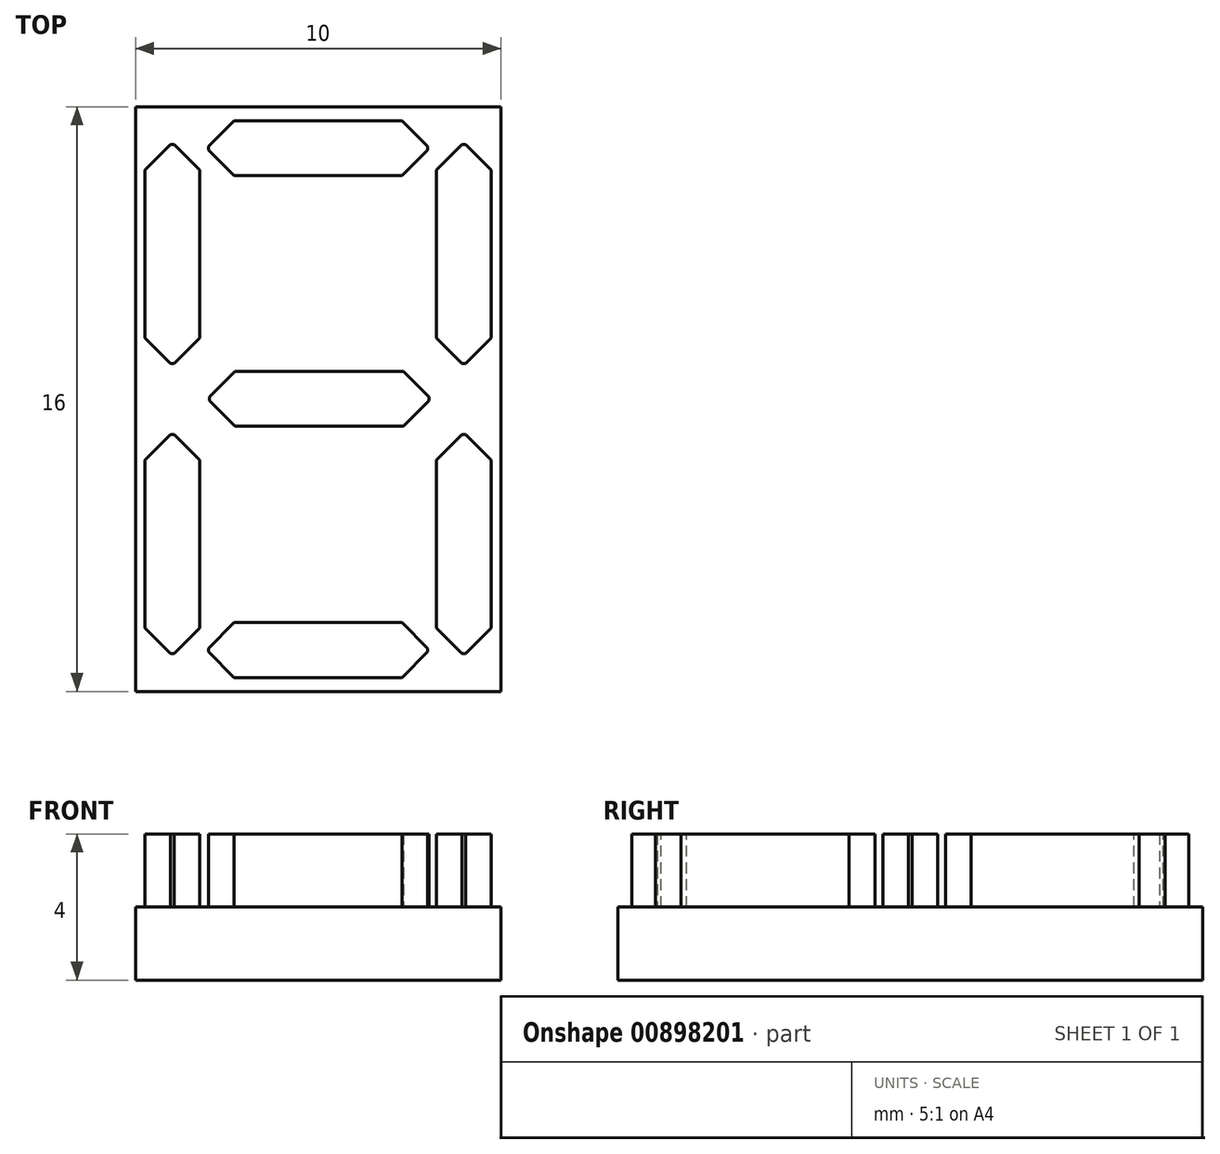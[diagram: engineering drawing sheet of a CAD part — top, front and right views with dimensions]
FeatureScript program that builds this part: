
annotation { "Feature Type Name" : "Feature", "Feature Type Description" : "" }
export const myFeature = defineFeature(function(context is Context, id is Id, definition is map)
    precondition{}
    {
        {
            var Q0;
            Q0=qCreatedBy(makeId("Top.planeOp"),FACE);
            var sketch = newSketch(context, id + "F0", { "sketchPlane" : qUnion([Q0])});
            skLineSegment(sketch, "E0.bottom", {"start": v(5, -8) * mm, "end": v(-5, -8) * mm});
            skLineSegment(sketch, "E0.top", {"start": v(5, 8) * mm, "end": v(-5, 8) * mm});
            skLineSegment(sketch, "E0.left", {"start": v(5, -8) * mm, "end": v(5, 8) * mm});
            skLineSegment(sketch, "E0.right", {"start": v(-5, -8) * mm, "end": v(-5, 8) * mm});
            skPoint(sketch, "E0.middle", {"position": v(0, 0) * mm});
            skSolve(sketch);
        }
        {
            var Q0;
            Q0 = qSketchRegion(id + "F0", true);
            extrude(context, id + "F1", {"entities" : qUnion([Q0]), "oppositeDirection" : true, "depth" : 2 * mm, "offsetDistance" : 25 * mm});
        }
        {
            var Q0;
            Q0=makeQuery(id+"F1.opExtrude","CAP_FACE",FACE,{"disambiguationData":[OSD([sQuery(id+"F0.wireOp",EDGE,"E0.bottom"),sQuery(id+"F0.wireOp",EDGE,"E0.top"),sQuery(id+"F0.wireOp",EDGE,"E0.left"),sQuery(id+"F0.wireOp",EDGE,"E0.right")])],"isStart":true});
            var sketch = newSketch(context, id + "F2", { "sketchPlane" : qUnion([Q0])});
            skLineSegment(sketch, "E1", {"start": v(0, 8) * mm, "end": v(0, -8) * mm, "construction": true});
            skLineSegment(sketch, "E2", {"start": v(-5, 0) * mm, "end": v(5, 0) * mm, "construction": true});
            skLineSegment(sketch, "E3.bottom", {"start": v(3, 6.12) * mm, "end": v(-3, 6.12) * mm});
            skLineSegment(sketch, "E3.top", {"start": v(3, 7.62) * mm, "end": v(-3, 7.62) * mm});
            skLineSegment(sketch, "E3.left", {"start": v(3, 6.12) * mm, "end": v(3, 7.62) * mm});
            skLineSegment(sketch, "E3.right", {"start": v(-3, 6.12) * mm, "end": v(-3, 7.62) * mm});
            skPoint(sketch, "E3.middle", {"position": v(0, 6.87) * mm});
            skLineSegment(sketch, "E4.MirrorCS", {"start": v(-3, -6.12) * mm, "end": v(-3, -7.62) * mm});
            skLineSegment(sketch, "E5.MirrorCS", {"start": v(3, -6.12) * mm, "end": v(3, -7.62) * mm});
            skPoint(sketch, "E6.MirrorP", {"position": v(0, -6.87) * mm});
            skLineSegment(sketch, "E7.MirrorCS", {"start": v(3, -6.12) * mm, "end": v(-3, -6.12) * mm});
            skLineSegment(sketch, "E8.MirrorCS", {"start": v(4.74, -6.97) * mm, "end": v(4.74, -0.97) * mm});
            skLineSegment(sketch, "E9.MirrorCS", {"start": v(3, -7.62) * mm, "end": v(-3, -7.62) * mm});
            skLineSegment(sketch, "E10.MirrorCS", {"start": v(3.24, -6.97) * mm, "end": v(3.24, -0.47) * mm});
            skLineSegment(sketch, "E11.MirrorCS", {"start": v(3.24, -0.97) * mm, "end": v(4.74, -0.97) * mm});
            skLineSegment(sketch, "E12.MirrorCS", {"start": v(3.24, -6.97) * mm, "end": v(4.74, -6.97) * mm});
            skPoint(sketch, "E13.middle", {"position": v(0, 0) * mm});
            skLineSegment(sketch, "E14.MirrorCS", {"start": v(-4.74, -6.97) * mm, "end": v(-4.74, -0.97) * mm});
            skLineSegment(sketch, "E15.MirrorCS", {"start": v(-3.24, -0.97) * mm, "end": v(-4.74, -0.97) * mm});
            skLineSegment(sketch, "E16.MirrorCS", {"start": v(-3.24, -6.97) * mm, "end": v(-3.24, -0.47) * mm});
            skLineSegment(sketch, "E17.MirrorCS", {"start": v(-3.24, -6.97) * mm, "end": v(-4.74, -6.97) * mm});
            skLineSegment(sketch, "E18.MirrorCS", {"start": v(-3.24, 0.97) * mm, "end": v(-4.74, 0.97) * mm});
            skLineSegment(sketch, "E19.MirrorCS", {"start": v(4.74, 6.97) * mm, "end": v(4.74, 0.97) * mm});
            skLineSegment(sketch, "E20.MirrorCS", {"start": v(3.24, 0.97) * mm, "end": v(4.74, 0.97) * mm});
            skLineSegment(sketch, "E21.MirrorCS", {"start": v(3.24, 6.97) * mm, "end": v(4.74, 6.97) * mm});
            skLineSegment(sketch, "E22.MirrorCS", {"start": v(-4.74, 6.97) * mm, "end": v(-4.74, 0.97) * mm});
            skLineSegment(sketch, "E23.MirrorCS", {"start": v(3.24, 6.97) * mm, "end": v(3.24, 0.47) * mm});
            skLineSegment(sketch, "E24.MirrorCS", {"start": v(-3.24, 6.97) * mm, "end": v(-3.24, 0.47) * mm});
            skLineSegment(sketch, "E25.MirrorCS", {"start": v(-3.24, 6.97) * mm, "end": v(-4.74, 6.97) * mm});
            skLineSegment(sketch, "E26.MirrorCS", {"start": v(-2.97, 0.76) * mm, "end": v(-2.97, -0.74) * mm});
            skLineSegment(sketch, "E27.MirrorCS", {"start": v(3.03, 0.76) * mm, "end": v(3.03, -0.74) * mm});
            skLineSegment(sketch, "E28.MirrorCS", {"start": v(3.03, 0.76) * mm, "end": v(-2.97, 0.76) * mm});
            skLineSegment(sketch, "E29.MirrorCS", {"start": v(3.03, -0.74) * mm, "end": v(-2.97, -0.74) * mm});
            skSolve(sketch);
        }
        {
            var Q0;
            Q0=makeQuery(id+"F2.imprint","IMPRINT",FACE,{"disambiguationData":[TD([[makeQuery(id+"F2.imprint","IMPRINT",EDGE,{"derivedFrom":sQuery(id+"F2.wireOp",EDGE,"E18.MirrorCS")}),-1.0]])]});
            var Q1;
            Q1=makeQuery(id+"F2.imprint","IMPRINT",FACE,{"disambiguationData":[TD([[makeQuery(id+"F2.imprint","IMPRINT",EDGE,{"derivedFrom":sQuery(id+"F2.wireOp",EDGE,"E3.top")}),1.0]])]});
            var Q2;
            Q2=makeQuery(id+"F2.imprint","IMPRINT",FACE,{"disambiguationData":[TD([[makeQuery(id+"F2.imprint","IMPRINT",EDGE,{"derivedFrom":sQuery(id+"F2.wireOp",EDGE,"E19.MirrorCS")}),-1.0]])]});
            var Q3;
            Q3=makeQuery(id+"F2.imprint","IMPRINT",FACE,{"disambiguationData":[TD([[makeQuery(id+"F2.imprint","IMPRINT",EDGE,{"derivedFrom":sQuery(id+"F2.wireOp",EDGE,"E26.MirrorCS")}),1.0]])]});
            var Q4;
            Q4=makeQuery(id+"F2.imprint","IMPRINT",FACE,{"disambiguationData":[TD([[makeQuery(id+"F2.imprint","IMPRINT",EDGE,{"derivedFrom":sQuery(id+"F2.wireOp",EDGE,"E14.MirrorCS")}),-1.0]])]});
            var Q5;
            Q5=makeQuery(id+"F2.imprint","IMPRINT",FACE,{"disambiguationData":[TD([[makeQuery(id+"F2.imprint","IMPRINT",EDGE,{"derivedFrom":sQuery(id+"F2.wireOp",EDGE,"E4.MirrorCS")}),1.0]])]});
            var Q6;
            Q6=makeQuery(id+"F2.imprint","IMPRINT",FACE,{"disambiguationData":[TD([[makeQuery(id+"F2.imprint","IMPRINT",EDGE,{"derivedFrom":sQuery(id+"F2.wireOp",EDGE,"E8.MirrorCS")}),1.0]])]});
            extrude(context, id + "F3", {"entities" : qUnion([Q0, Q1, Q2, Q3, Q4, Q5, Q6]), "operationType" : NewBodyOperationType.ADD, "depth" : 2 * mm, "offsetDistance" : 25 * mm});
        }
        {
            var Q0;
            Q0=makeQuery(id+"F3.opExtrude","SWEPT_EDGE",EDGE,{"disambiguationData":[OSD([sQuery(id+"F2.wireOp",EDGE,"E3.left"),sQuery(id+"F2.wireOp",EDGE,"E3.bottom")])]});
            var Q1;
            Q1=makeQuery(id+"F3.opExtrude","SWEPT_EDGE",EDGE,{"disambiguationData":[OSD([sQuery(id+"F2.wireOp",EDGE,"E21.MirrorCS"),sQuery(id+"F2.wireOp",EDGE,"E23.MirrorCS")])]});
            var Q2;
            Q2=makeQuery(id+"F3.opExtrude","SWEPT_EDGE",EDGE,{"disambiguationData":[OSD([sQuery(id+"F2.wireOp",EDGE,"E20.MirrorCS"),sQuery(id+"F2.wireOp",EDGE,"E23.MirrorCS")])]});
            var Q3;
            Q3=makeQuery(id+"F3.opExtrude","SWEPT_EDGE",EDGE,{"disambiguationData":[OSD([sQuery(id+"F2.wireOp",EDGE,"E19.MirrorCS"),sQuery(id+"F2.wireOp",EDGE,"E20.MirrorCS")])]});
            var Q4;
            Q4=makeQuery(id+"F3.opExtrude","SWEPT_EDGE",EDGE,{"disambiguationData":[OSD([sQuery(id+"F2.wireOp",EDGE,"E10.MirrorCS"),sQuery(id+"F2.wireOp",EDGE,"E11.MirrorCS")])]});
            var Q5;
            Q5=makeQuery(id+"F3.opExtrude","SWEPT_EDGE",EDGE,{"disambiguationData":[OSD([sQuery(id+"F2.wireOp",EDGE,"E27.MirrorCS"),sQuery(id+"F2.wireOp",EDGE,"E29.MirrorCS")])]});
            var Q6;
            Q6=makeQuery(id+"F3.opExtrude","SWEPT_EDGE",EDGE,{"disambiguationData":[OSD([sQuery(id+"F2.wireOp",EDGE,"E26.MirrorCS"),sQuery(id+"F2.wireOp",EDGE,"E29.MirrorCS")])]});
            var Q7;
            Q7=makeQuery(id+"F3.opExtrude","SWEPT_EDGE",EDGE,{"disambiguationData":[OSD([sQuery(id+"F2.wireOp",EDGE,"E26.MirrorCS"),sQuery(id+"F2.wireOp",EDGE,"E28.MirrorCS")])]});
            var Q8;
            Q8=makeQuery(id+"F3.opExtrude","SWEPT_EDGE",EDGE,{"disambiguationData":[OSD([sQuery(id+"F2.wireOp",EDGE,"E18.MirrorCS"),sQuery(id+"F2.wireOp",EDGE,"E24.MirrorCS")])]});
            var Q9;
            Q9=makeQuery(id+"F3.opExtrude","SWEPT_EDGE",EDGE,{"disambiguationData":[OSD([sQuery(id+"F2.wireOp",EDGE,"E18.MirrorCS"),sQuery(id+"F2.wireOp",EDGE,"E22.MirrorCS")])]});
            var Q10;
            Q10=makeQuery(id+"F3.opExtrude","SWEPT_EDGE",EDGE,{"disambiguationData":[OSD([sQuery(id+"F2.wireOp",EDGE,"E22.MirrorCS"),sQuery(id+"F2.wireOp",EDGE,"E25.MirrorCS")])]});
            var Q11;
            Q11=makeQuery(id+"F3.opExtrude","SWEPT_EDGE",EDGE,{"disambiguationData":[OSD([sQuery(id+"F2.wireOp",EDGE,"E3.right"),sQuery(id+"F2.wireOp",EDGE,"E3.bottom")])]});
            var Q12;
            Q12=makeQuery(id+"F3.opExtrude","SWEPT_EDGE",EDGE,{"disambiguationData":[OSD([sQuery(id+"F2.wireOp",EDGE,"E3.top"),sQuery(id+"F2.wireOp",EDGE,"E3.right")])]});
            var Q13;
            Q13=makeQuery(id+"F3.opExtrude","SWEPT_EDGE",EDGE,{"disambiguationData":[OSD([sQuery(id+"F2.wireOp",EDGE,"E10.MirrorCS"),sQuery(id+"F2.wireOp",EDGE,"E12.MirrorCS")])]});
            var Q14;
            Q14=makeQuery(id+"F3.opExtrude","SWEPT_EDGE",EDGE,{"disambiguationData":[OSD([sQuery(id+"F2.wireOp",EDGE,"E8.MirrorCS"),sQuery(id+"F2.wireOp",EDGE,"E12.MirrorCS")])]});
            var Q15;
            Q15=makeQuery(id+"F3.opExtrude","SWEPT_EDGE",EDGE,{"disambiguationData":[OSD([sQuery(id+"F2.wireOp",EDGE,"E5.MirrorCS"),sQuery(id+"F2.wireOp",EDGE,"E9.MirrorCS")])]});
            var Q16;
            Q16=makeQuery(id+"F3.opExtrude","SWEPT_EDGE",EDGE,{"disambiguationData":[OSD([sQuery(id+"F2.wireOp",EDGE,"E4.MirrorCS"),sQuery(id+"F2.wireOp",EDGE,"E9.MirrorCS")])]});
            var Q17;
            Q17=makeQuery(id+"F3.opExtrude","SWEPT_EDGE",EDGE,{"disambiguationData":[OSD([sQuery(id+"F2.wireOp",EDGE,"E16.MirrorCS"),sQuery(id+"F2.wireOp",EDGE,"E17.MirrorCS")])]});
            var Q18;
            Q18=makeQuery(id+"F3.opExtrude","SWEPT_EDGE",EDGE,{"disambiguationData":[OSD([sQuery(id+"F2.wireOp",EDGE,"E14.MirrorCS"),sQuery(id+"F2.wireOp",EDGE,"E17.MirrorCS")])]});
            var Q19;
            Q19=makeQuery(id+"F3.opExtrude","SWEPT_EDGE",EDGE,{"disambiguationData":[OSD([sQuery(id+"F2.wireOp",EDGE,"E4.MirrorCS"),sQuery(id+"F2.wireOp",EDGE,"E7.MirrorCS")])]});
            var Q20;
            Q20=makeQuery(id+"F3.opExtrude","SWEPT_EDGE",EDGE,{"disambiguationData":[OSD([sQuery(id+"F2.wireOp",EDGE,"E14.MirrorCS"),sQuery(id+"F2.wireOp",EDGE,"E15.MirrorCS")])]});
            var Q21;
            Q21=makeQuery(id+"F3.opExtrude","SWEPT_EDGE",EDGE,{"disambiguationData":[OSD([sQuery(id+"F2.wireOp",EDGE,"E15.MirrorCS"),sQuery(id+"F2.wireOp",EDGE,"E16.MirrorCS")])]});
            var Q22;
            Q22=makeQuery(id+"F3.opExtrude","SWEPT_EDGE",EDGE,{"disambiguationData":[OSD([sQuery(id+"F2.wireOp",EDGE,"E27.MirrorCS"),sQuery(id+"F2.wireOp",EDGE,"E28.MirrorCS")])]});
            var Q23;
            Q23=makeQuery(id+"F3.opExtrude","SWEPT_EDGE",EDGE,{"disambiguationData":[OSD([sQuery(id+"F2.wireOp",EDGE,"E8.MirrorCS"),sQuery(id+"F2.wireOp",EDGE,"E11.MirrorCS")])]});
            var Q24;
            Q24=makeQuery(id+"F3.opExtrude","SWEPT_EDGE",EDGE,{"disambiguationData":[OSD([sQuery(id+"F2.wireOp",EDGE,"E5.MirrorCS"),sQuery(id+"F2.wireOp",EDGE,"E7.MirrorCS")])]});
            var Q25;
            Q25=makeQuery(id+"F3.opExtrude","SWEPT_EDGE",EDGE,{"disambiguationData":[OSD([sQuery(id+"F2.wireOp",EDGE,"E19.MirrorCS"),sQuery(id+"F2.wireOp",EDGE,"E21.MirrorCS")])]});
            var Q26;
            Q26=makeQuery(id+"F3.opExtrude","SWEPT_EDGE",EDGE,{"disambiguationData":[OSD([sQuery(id+"F2.wireOp",EDGE,"E3.top"),sQuery(id+"F2.wireOp",EDGE,"E3.left")])]});
            var Q27;
            Q27=makeQuery(id+"F3.opExtrude","SWEPT_EDGE",EDGE,{"disambiguationData":[OSD([sQuery(id+"F2.wireOp",EDGE,"E24.MirrorCS"),sQuery(id+"F2.wireOp",EDGE,"E25.MirrorCS")])]});
            chamfer(context, id + "F4", {"entities" : qUnion([Q0, Q1, Q2, Q3, Q4, Q5, Q6, Q7, Q8, Q9, Q10, Q11, Q12, Q13, Q14, Q15, Q16, Q17, Q18, Q19, Q20, Q21, Q22, Q23, Q24, Q25, Q26, Q27]), "width" : 0.7 * mm, "tangentPropagation" : true});
        }
    });
